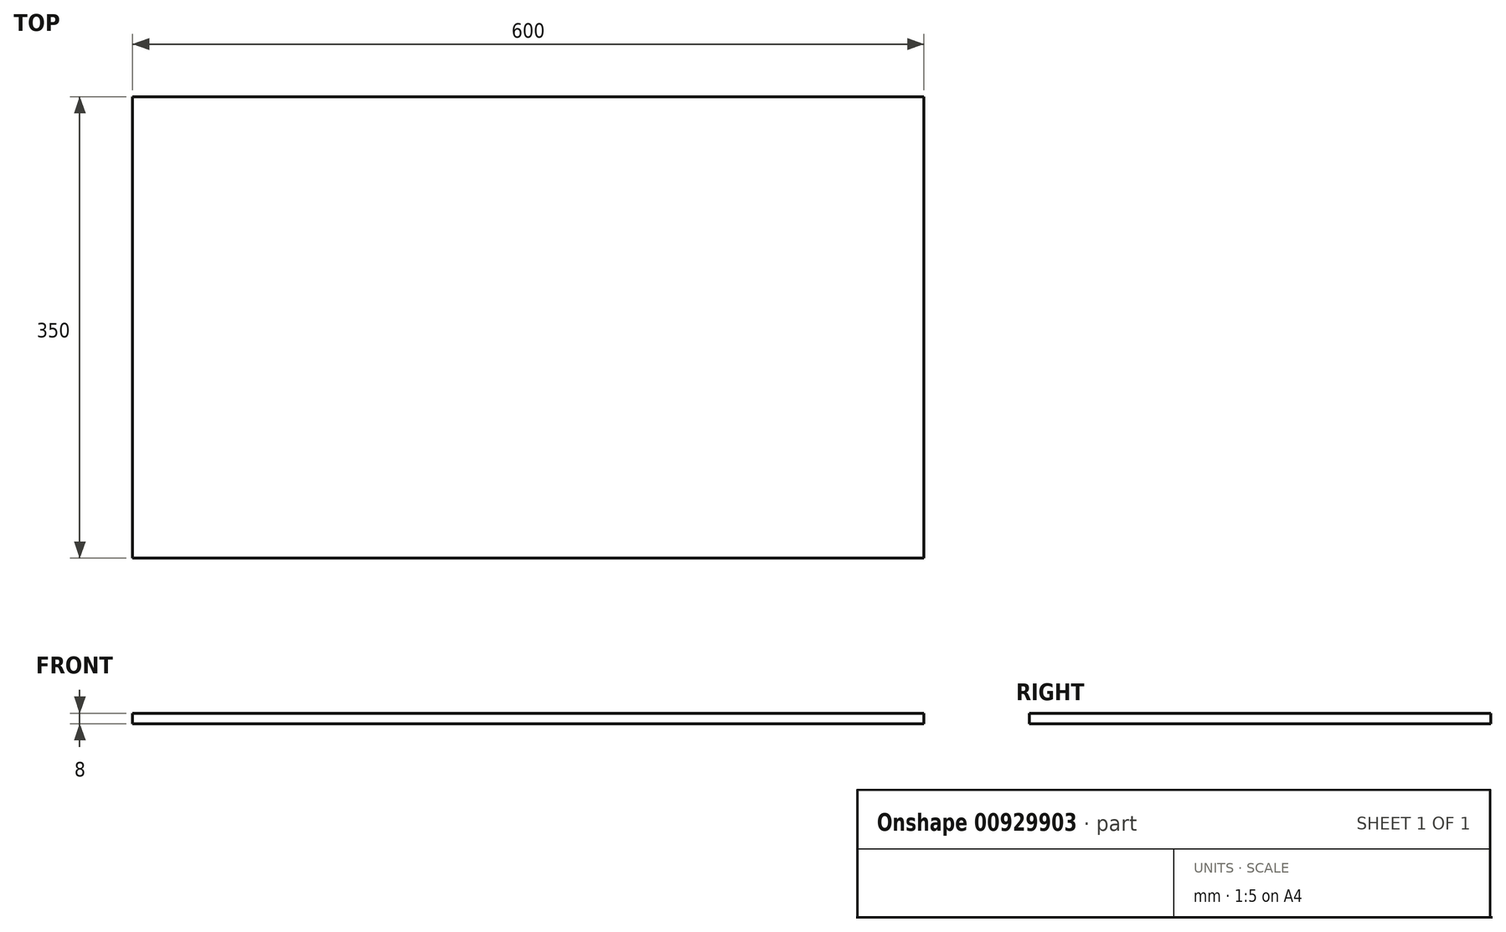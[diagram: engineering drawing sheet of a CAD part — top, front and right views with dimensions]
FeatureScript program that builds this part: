
annotation { "Feature Type Name" : "Feature", "Feature Type Description" : "" }
export const myFeature = defineFeature(function(context is Context, id is Id, definition is map)
    precondition{}
    {
        {
            var Q0;
            Q0=qCreatedBy(makeId("Top.planeOp"),FACE);
            var sketch = newSketch(context, id + "F0", { "sketchPlane" : qUnion([Q0])});
            skLineSegment(sketch, "E0.bottom", {"start": v(0, 0) * mm, "end": v(600, 0) * mm});
            skLineSegment(sketch, "E0.top", {"start": v(0, 350) * mm, "end": v(600, 350) * mm});
            skLineSegment(sketch, "E0.left", {"start": v(0, 0) * mm, "end": v(0, 350) * mm});
            skLineSegment(sketch, "E0.right", {"start": v(600, 0) * mm, "end": v(600, 350) * mm});
            skSolve(sketch);
        }
        {
            var Q0;
            Q0 = qSketchRegion(id + "F0", true);
            extrude(context, id + "F1", {"entities" : qUnion([Q0]), "depth" : 8 * mm, "offsetDistance" : 25 * mm});
        }
    });
